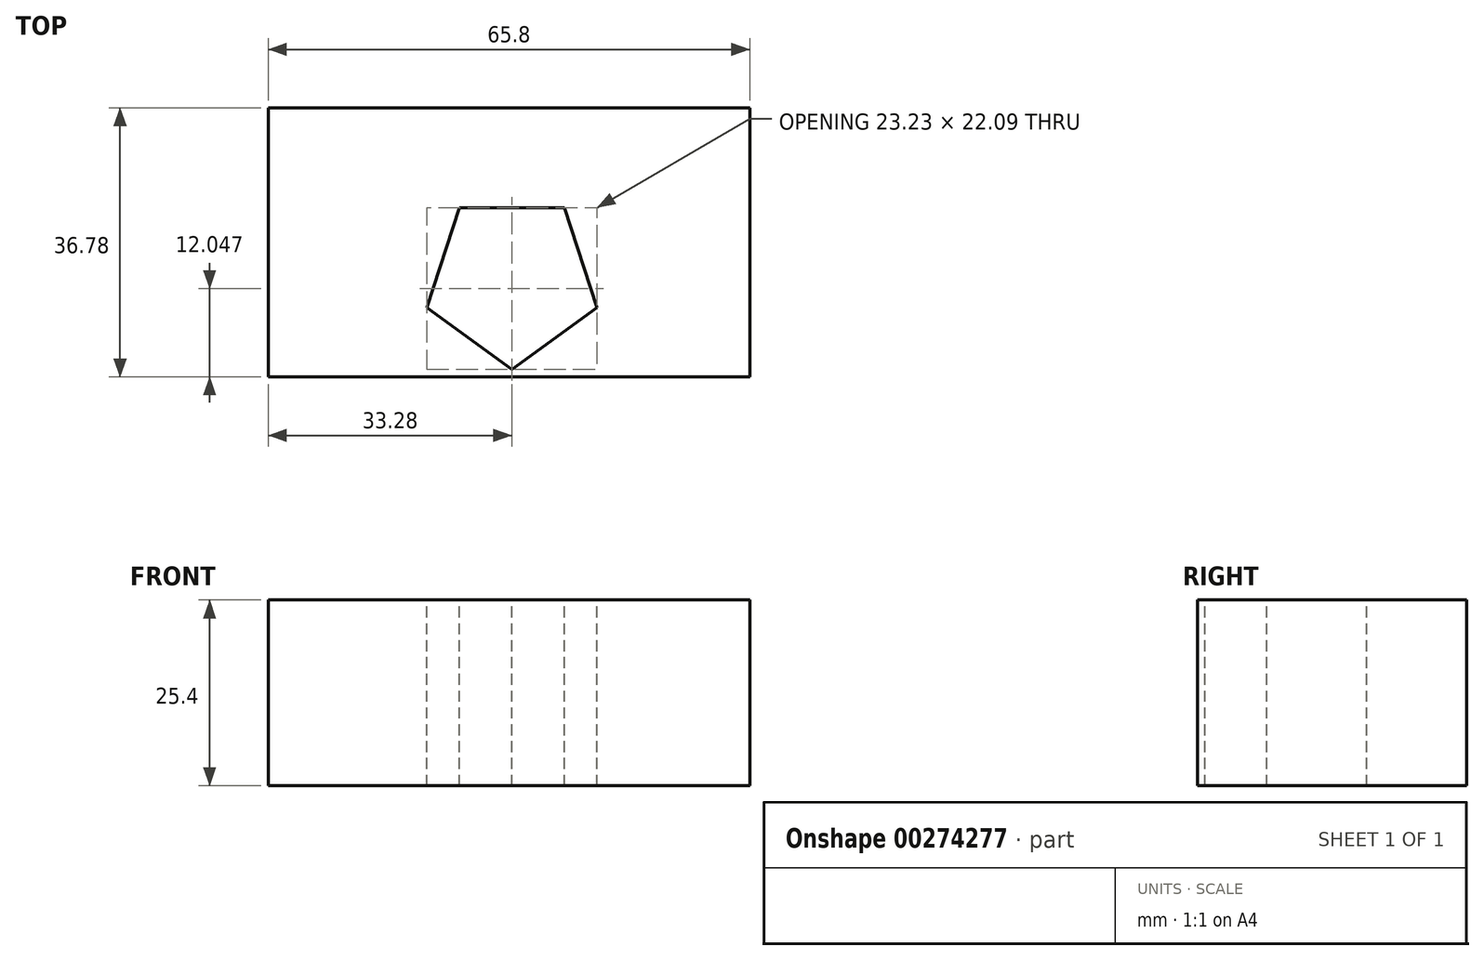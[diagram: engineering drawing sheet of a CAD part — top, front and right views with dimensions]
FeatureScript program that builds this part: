
annotation { "Feature Type Name" : "Feature", "Feature Type Description" : "" }
export const myFeature = defineFeature(function(context is Context, id is Id, definition is map)
    precondition{}
    {
        {
            var Q0;
            Q0=qCreatedBy(makeId("Top.planeOp"),FACE);
            var sketch = newSketch(context, id + "F0", { "sketchPlane" : qUnion([Q0])});
            skLineSegment(sketch, "E0.bottom", {"start": v(-33.28, 31.87) * mm, "end": v(32.52, 31.87) * mm});
            skLineSegment(sketch, "E0.top", {"start": v(-33.28, -4.91) * mm, "end": v(32.52, -4.91) * mm});
            skLineSegment(sketch, "E0.left", {"start": v(-33.28, 31.87) * mm, "end": v(-33.28, -4.91) * mm});
            skLineSegment(sketch, "E0.right", {"start": v(32.52, 31.87) * mm, "end": v(32.52, -4.91) * mm});
            skSolve(sketch);
        }
        {
            var Q0;
            Q0 = qSketchRegion(id + "F0", true);
            extrude(context, id + "F1", {"entities" : qUnion([Q0]), "depth" : 25.4 * mm});
        }
        {
            var Q0;
            Q0=makeQuery(id+"F1.opExtrude","CAP_FACE",FACE,{"disambiguationData":[OSD([sQuery(id+"F0.wireOp",EDGE,"E0.bottom"),sQuery(id+"F0.wireOp",EDGE,"E0.top"),sQuery(id+"F0.wireOp",EDGE,"E0.left"),sQuery(id+"F0.wireOp",EDGE,"E0.right")])],"isStart":false});
            var sketch = newSketch(context, id + "F2", { "sketchPlane" : qUnion([Q0])});
            skCircle(sketch, "E1.cCircle", {"center": v(0, 8.3) * mm, "radius": 9.88 * mm, "construction": true});
            skLineSegment(sketch, "E1.0", {"start": v(-7.18, 18.18) * mm, "end": v(7.18, 18.18) * mm});
            skLineSegment(sketch, "E1.1", {"start": v(7.18, 18.18) * mm, "end": v(11.61, 4.53) * mm});
            skLineSegment(sketch, "E1.2", {"start": v(11.61, 4.53) * mm, "end": v(0, -3.9) * mm});
            skLineSegment(sketch, "E1.3", {"start": v(0, -3.9) * mm, "end": v(-11.61, 4.53) * mm});
            skLineSegment(sketch, "E1.4", {"start": v(-11.61, 4.53) * mm, "end": v(-7.18, 18.18) * mm});
            skPoint(sketch, "E1.0.midPoint", {"position": v(0, 18.18) * mm});
            skSolve(sketch);
        }
        {
            var Q0;
            Q0=makeQuery(id+"F2.imprint","IMPRINT",FACE,{"disambiguationData":[TD([[makeQuery(id+"F2.imprint","IMPRINT",EDGE,{"derivedFrom":sQuery(id+"F2.wireOp",EDGE,"E1.0")}),-1.0]])]});
            extrude(context, id + "F3", {"entities" : qUnion([Q0]), "operationType" : NewBodyOperationType.REMOVE, "oppositeDirection" : true, "depth" : 25.4 * mm});
        }
    });
